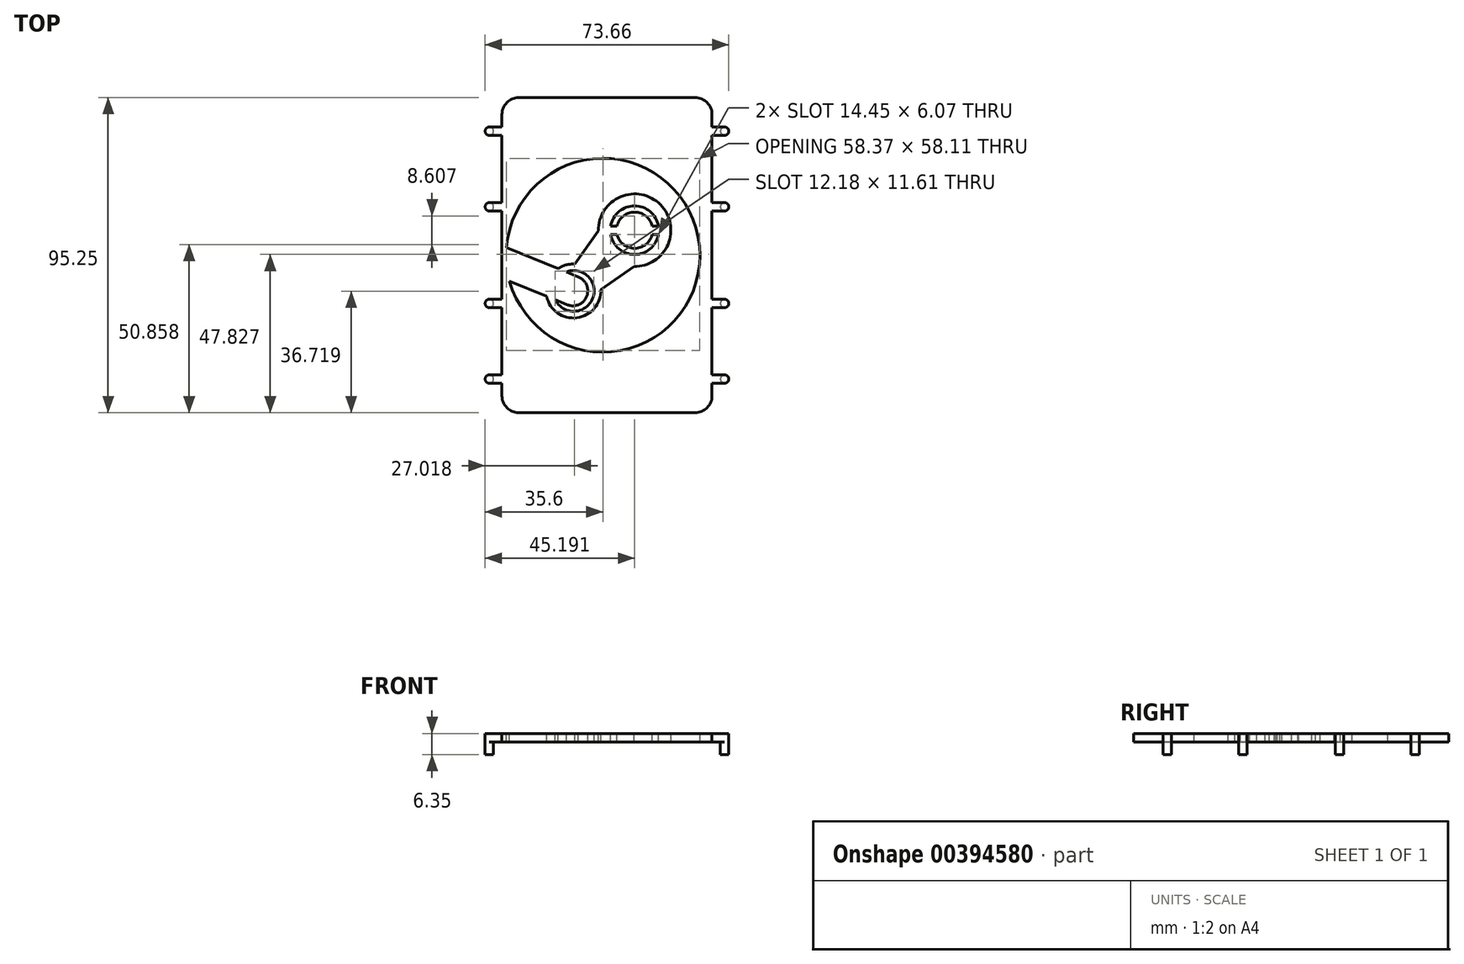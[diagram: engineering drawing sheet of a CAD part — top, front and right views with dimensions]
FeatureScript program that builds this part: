
annotation { "Feature Type Name" : "Feature", "Feature Type Description" : "" }
export const myFeature = defineFeature(function(context is Context, id is Id, definition is map)
    precondition{}
    {
        {
            var Q0;
            Q0=qCreatedBy(makeId("Top.planeOp"),FACE);
            var sketch = newSketch(context, id + "F0", { "sketchPlane" : qUnion([Q0])});
            skLineSegment(sketch, "E0.bottom", {"start": v(-63.5, 95.25) * mm, "end": v(0, 95.25) * mm});
            skLineSegment(sketch, "E0.top", {"start": v(-63.5, 0) * mm, "end": v(0, 0) * mm});
            skLineSegment(sketch, "E0.left", {"start": v(-63.5, 95.25) * mm, "end": v(-63.5, 0) * mm});
            skLineSegment(sketch, "E0.right", {"start": v(0, 95.25) * mm, "end": v(0, 0) * mm});
            skSolve(sketch);
        }
        {
            var Q0;
            Q0=makeQuery(id+"F0.imprint","IMPRINT",FACE,{"disambiguationData":[TD([[makeQuery(id+"F0.imprint","IMPRINT",EDGE,{"derivedFrom":sQuery(id+"F0.wireOp",EDGE,"E0.bottom")}),-1.0]])]});
            extrude(context, id + "F1", {"entities" : qUnion([Q0]), "depth" : 2.54 * mm});
        }
        {
            var Q0;
            Q0=makeQuery(id+"F1.opExtrude","SWEPT_EDGE",EDGE,{"disambiguationData":[OSD([sQuery(id+"F0.wireOp",EDGE,"E0.top"),sQuery(id+"F0.wireOp",EDGE,"E0.left")])]});
            var Q1;
            Q1=makeQuery(id+"F1.opExtrude","SWEPT_EDGE",EDGE,{"disambiguationData":[OSD([sQuery(id+"F0.wireOp",EDGE,"E0.top"),sQuery(id+"F0.wireOp",EDGE,"E0.right")])]});
            var Q2;
            Q2=makeQuery(id+"F1.opExtrude","SWEPT_EDGE",EDGE,{"disambiguationData":[OSD([sQuery(id+"F0.wireOp",EDGE,"E0.bottom"),sQuery(id+"F0.wireOp",EDGE,"E0.right")])]});
            var Q3;
            Q3=makeQuery(id+"F1.opExtrude","SWEPT_EDGE",EDGE,{"disambiguationData":[OSD([sQuery(id+"F0.wireOp",EDGE,"E0.bottom"),sQuery(id+"F0.wireOp",EDGE,"E0.left")])]});
            fillet(context, id + "F2", {"entities" : qUnion([Q0, Q1, Q2, Q3]), "radius" : 5.08 * mm, "tangentPropagation" : true, "allowEdgeOverflow" : false});
        }
        {
            var Q0;
            Q0=makeQuery(id+"F1.opExtrude","CAP_FACE",FACE,{"disambiguationData":[OSD([sQuery(id+"F0.wireOp",EDGE,"E0.bottom"),sQuery(id+"F0.wireOp",EDGE,"E0.top"),sQuery(id+"F0.wireOp",EDGE,"E0.left"),sQuery(id+"F0.wireOp",EDGE,"E0.right")])],"isStart":false});
            var sketch = newSketch(context, id + "F3", { "sketchPlane" : qUnion([Q0])});
            skPoint(sketch, "E1", {"position": v(0, 47.63) * mm});
            skLineSegment(sketch, "E2", {"start": v(-62.17, 49.9) * mm, "end": v(-46.54, 43.5) * mm});
            skArc(sketch, "E3", {"start": v(-41.49, 44.9) * mm, "mid": v(-44.14, 44.65) * mm, "end": v(-46.54, 43.5) * mm});
            skLineSegment(sketch, "E4", {"start": v(-41.49, 44.9) * mm, "end": v(-34.35, 55.05) * mm});
            skArc(sketch, "E5", {"start": v(-23.6, 44.2) * mm, "mid": v(-15.6, 62.88) * mm, "end": v(-34.35, 55.05) * mm});
            skCircle(sketch, "E6", {"center": v(-23.39, 55.16) * mm, "radius": 5.47 * mm});
            skCircle(sketch, "E7", {"center": v(-23.39, 55.16) * mm, "radius": 7.34 * mm});
            skLineSegment(sketch, "E8", {"start": v(-23.6, 44.2) * mm, "end": v(-33.57, 37.24) * mm});
            skArc(sketch, "E9", {"start": v(-49.98, 35.15) * mm, "mid": v(-40.82, 28.7) * mm, "end": v(-33.57, 37.24) * mm});
            skLineSegment(sketch, "E10", {"start": v(-49.98, 35.15) * mm, "end": v(-61.2, 39.82) * mm});
            skArc(sketch, "E11", {"start": v(-61.2, 39.82) * mm, "mid": v(-3.8, 50.35) * mm, "end": v(-62.17, 49.9) * mm});
            skLineSegment(sketch, "E12", {"start": v(-44, 42.55) * mm, "end": v(-40.45, 41.06) * mm});
            skLineSegment(sketch, "E13", {"start": v(-47.37, 34.15) * mm, "end": v(-43.83, 32.66) * mm});
            skArc(sketch, "E14", {"start": v(-43.83, 32.66) * mm, "mid": v(-37.87, 35.15) * mm, "end": v(-40.45, 41.06) * mm});
            skArc(sketch, "E15", {"start": v(-47.37, 34.15) * mm, "mid": v(-36.08, 34.5) * mm, "end": v(-44, 42.55) * mm});
            skLineSegment(sketch, "E16", {"start": v(-30.62, 56.43) * mm, "end": v(-28.71, 56.43) * mm});
            skLineSegment(sketch, "E17", {"start": v(-30.62, 53.9) * mm, "end": v(-28.71, 53.9) * mm});
            skLineSegment(sketch, "E18", {"start": v(-16.16, 53.9) * mm, "end": v(-18.06, 53.9) * mm});
            skLineSegment(sketch, "E19", {"start": v(-18.06, 56.43) * mm, "end": v(-16.16, 56.43) * mm});
            skSolve(sketch);
        }
        {
            var Q0;
            {var subQ0=sQuery(id+"F3.wireOp",EDGE,"E16");Q0=makeQuery(id+"F3.imprint","IMPRINT",FACE,{"disambiguationData":[TD([[makeQuery(id+"F3.imprint","IMPRINT",EDGE,{"derivedFrom":subQ0}),1.0]])]});}
            var Q1;
            {var subQ0=sQuery(id+"F3.wireOp",EDGE,"E17");Q1=makeQuery(id+"F3.imprint","IMPRINT",FACE,{"disambiguationData":[TD([[makeQuery(id+"F3.imprint","IMPRINT",EDGE,{"derivedFrom":subQ0}),-1.0]])]});}
            var Q2;
            Q2=makeQuery(id+"F3.imprint","IMPRINT",FACE,{"disambiguationData":[TD([[makeQuery(id+"F3.imprint","IMPRINT",EDGE,{"derivedFrom":sQuery(id+"F3.wireOp",EDGE,"E2")}),1.0]])]});
            var Q3;
            Q3=makeQuery(id+"F3.imprint","IMPRINT",FACE,{"disambiguationData":[TD([[makeQuery(id+"F3.imprint","IMPRINT",EDGE,{"derivedFrom":sQuery(id+"F3.wireOp",EDGE,"E12")}),1.0]])]});
            extrude(context, id + "F4", {"entities" : qUnion([Q0, Q1, Q2, Q3]), "operationType" : NewBodyOperationType.REMOVE, "endBound" : BoundingType.THROUGH_ALL, "oppositeDirection" : true, "depth" : 2.54 * mm});
        }
        {
            var Q0;
            {var subQ0=sQuery(id+"F0.wireOp",EDGE,"E0.right");var subQ1=sQuery(id+"F0.wireOp",EDGE,"E0.top");var subQ2=sQuery(id+"F0.wireOp",EDGE,"E0.left");var subQ3=sQuery(id+"F0.wireOp",EDGE,"E0.bottom");Q0=makeQuery(id+"F4.boolean.opBoolean","SPLIT",FACE,{"disambiguationData":[TD([makeQuery(id+"F1.opExtrude","SWEPT_FACE",FACE,{"disambiguationData":[OSD([subQ3])]})])],"derivedFrom":makeQuery(id+"F1.opExtrude","CAP_FACE",FACE,{"disambiguationData":[OSD([subQ3,subQ1,subQ2,subQ0])],"isStart":true})});}
            var sketch = newSketch(context, id + "F5", { "sketchPlane" : qUnion([Q0])});
            skCircle(sketch, "E20", {"center": v(-67.31, -10.16) * mm, "radius": 1.27 * mm});
            skCircle(sketch, "E21", {"center": v(-67.31, -33.02) * mm, "radius": 1.27 * mm});
            skCircle(sketch, "E22", {"center": v(-67.31, -62.23) * mm, "radius": 1.27 * mm});
            skCircle(sketch, "E23", {"center": v(-67.31, -85.1) * mm, "radius": 1.27 * mm});
            skCircle(sketch, "E24", {"center": v(3.8, -85.1) * mm, "radius": 1.27 * mm});
            skCircle(sketch, "E25", {"center": v(3.8, -62.23) * mm, "radius": 1.27 * mm});
            skCircle(sketch, "E26", {"center": v(3.8, -33.02) * mm, "radius": 1.27 * mm});
            skCircle(sketch, "E27", {"center": v(3.8, -10.16) * mm, "radius": 1.27 * mm});
            skLineSegment(sketch, "E28", {"start": v(-67.31, -86.36) * mm, "end": v(-63.5, -86.36) * mm});
            skLineSegment(sketch, "E29", {"start": v(-63.5, -86.36) * mm, "end": v(-63.5, -83.82) * mm});
            skLineSegment(sketch, "E30", {"start": v(-63.5, -83.82) * mm, "end": v(-67.31, -83.82) * mm});
            skLineSegment(sketch, "E31", {"start": v(-67.31, -63.5) * mm, "end": v(-63.5, -63.5) * mm});
            skLineSegment(sketch, "E32", {"start": v(-63.5, -63.5) * mm, "end": v(-63.5, -60.96) * mm});
            skLineSegment(sketch, "E33", {"start": v(-63.5, -60.96) * mm, "end": v(-67.31, -60.96) * mm});
            skLineSegment(sketch, "E34", {"start": v(-67.31, -34.3) * mm, "end": v(-63.5, -34.3) * mm});
            skLineSegment(sketch, "E35", {"start": v(-63.5, -34.3) * mm, "end": v(-63.5, -31.75) * mm});
            skLineSegment(sketch, "E36", {"start": v(-63.5, -31.75) * mm, "end": v(-67.31, -31.75) * mm});
            skLineSegment(sketch, "E37", {"start": v(-67.31, -11.43) * mm, "end": v(-63.5, -11.43) * mm});
            skLineSegment(sketch, "E38", {"start": v(-67.31, -8.9) * mm, "end": v(-63.5, -8.9) * mm});
            skLineSegment(sketch, "E39", {"start": v(-63.5, -8.9) * mm, "end": v(-63.5, -11.43) * mm});
            skLineSegment(sketch, "E40", {"start": v(3.8, -11.43) * mm, "end": v(0, -11.43) * mm});
            skLineSegment(sketch, "E41", {"start": v(0, -11.43) * mm, "end": v(0, -8.9) * mm});
            skLineSegment(sketch, "E42", {"start": v(0, -8.9) * mm, "end": v(3.8, -8.9) * mm});
            skLineSegment(sketch, "E43", {"start": v(3.8, -34.3) * mm, "end": v(0, -34.3) * mm});
            skLineSegment(sketch, "E44", {"start": v(0, -34.3) * mm, "end": v(0, -31.75) * mm});
            skLineSegment(sketch, "E45", {"start": v(0, -31.75) * mm, "end": v(3.8, -31.75) * mm});
            skLineSegment(sketch, "E46", {"start": v(3.8, -63.5) * mm, "end": v(0, -63.5) * mm});
            skLineSegment(sketch, "E47", {"start": v(0, -63.5) * mm, "end": v(0, -60.96) * mm});
            skLineSegment(sketch, "E48", {"start": v(0, -60.96) * mm, "end": v(3.8, -60.96) * mm});
            skLineSegment(sketch, "E49", {"start": v(3.8, -83.82) * mm, "end": v(0, -83.82) * mm});
            skLineSegment(sketch, "E50", {"start": v(0, -86.36) * mm, "end": v(0, -83.82) * mm});
            skLineSegment(sketch, "E51", {"start": v(0, -86.36) * mm, "end": v(3.8, -86.36) * mm});
            skSolve(sketch);
        }
        {
            var Q0;
            {var subQ0=sQuery(id+"F5.wireOp",EDGE,"E28");Q0=makeQuery(id+"F5.imprint","IMPRINT",FACE,{"disambiguationData":[TD([[makeQuery(id+"F5.imprint","IMPRINT",EDGE,{"derivedFrom":subQ0}),1.0]])]});}
            var Q1;
            {var subQ0=sQuery(id+"F5.wireOp",EDGE,"E31");Q1=makeQuery(id+"F5.imprint","IMPRINT",FACE,{"disambiguationData":[TD([[makeQuery(id+"F5.imprint","IMPRINT",EDGE,{"derivedFrom":subQ0}),1.0]])]});}
            var Q2;
            {var subQ0=sQuery(id+"F5.wireOp",EDGE,"E34");Q2=makeQuery(id+"F5.imprint","IMPRINT",FACE,{"disambiguationData":[TD([[makeQuery(id+"F5.imprint","IMPRINT",EDGE,{"derivedFrom":subQ0}),1.0]])]});}
            var Q3;
            {var subQ0=sQuery(id+"F5.wireOp",EDGE,"E37");Q3=makeQuery(id+"F5.imprint","IMPRINT",FACE,{"disambiguationData":[TD([[makeQuery(id+"F5.imprint","IMPRINT",EDGE,{"derivedFrom":subQ0}),1.0]])]});}
            var Q4;
            {var subQ0=sQuery(id+"F5.wireOp",EDGE,"E40");Q4=makeQuery(id+"F5.imprint","IMPRINT",FACE,{"disambiguationData":[TD([[makeQuery(id+"F5.imprint","IMPRINT",EDGE,{"derivedFrom":subQ0}),-1.0]])]});}
            var Q5;
            {var subQ0=sQuery(id+"F5.wireOp",EDGE,"E43");Q5=makeQuery(id+"F5.imprint","IMPRINT",FACE,{"disambiguationData":[TD([[makeQuery(id+"F5.imprint","IMPRINT",EDGE,{"derivedFrom":subQ0}),-1.0]])]});}
            var Q6;
            {var subQ0=sQuery(id+"F5.wireOp",EDGE,"E46");Q6=makeQuery(id+"F5.imprint","IMPRINT",FACE,{"disambiguationData":[TD([[makeQuery(id+"F5.imprint","IMPRINT",EDGE,{"derivedFrom":subQ0}),-1.0]])]});}
            var Q7;
            {var subQ0=sQuery(id+"F5.wireOp",EDGE,"E49");Q7=makeQuery(id+"F5.imprint","IMPRINT",FACE,{"disambiguationData":[TD([[makeQuery(id+"F5.imprint","IMPRINT",EDGE,{"derivedFrom":subQ0}),1.0]])]});}
            extrude(context, id + "F6", {"entities" : qUnion([Q0, Q1, Q2, Q3, Q4, Q5, Q6, Q7]), "operationType" : NewBodyOperationType.ADD, "oppositeDirection" : true, "depth" : 2.54 * mm});
        }
        {
            var Q0;
            {var subQ0=sQuery(id+"F5.wireOp",EDGE,"E23");var subQ1=makeQuery(id+"F5.imprint","INTERSECT",VERTEX,{"derivedFrom":[subQ0,sQuery(id+"F5.wireOp",EDGE,"E28")]});Q0=makeQuery(id+"F5.imprint","IMPRINT",FACE,{"disambiguationData":[TD([[makeQuery(id+"F5.imprint","IMPRINT",EDGE,{"disambiguationData":[TD([[subQ1,1.0]])],"derivedFrom":subQ0}),1.0]])]});}
            var Q1;
            {var subQ0=sQuery(id+"F5.wireOp",EDGE,"E22");var subQ1=makeQuery(id+"F5.imprint","INTERSECT",VERTEX,{"derivedFrom":[subQ0,sQuery(id+"F5.wireOp",EDGE,"E31")]});Q1=makeQuery(id+"F5.imprint","IMPRINT",FACE,{"disambiguationData":[TD([[makeQuery(id+"F5.imprint","IMPRINT",EDGE,{"disambiguationData":[TD([[subQ1,1.0]])],"derivedFrom":subQ0}),1.0]])]});}
            var Q2;
            {var subQ0=sQuery(id+"F5.wireOp",EDGE,"E21");var subQ1=makeQuery(id+"F5.imprint","INTERSECT",VERTEX,{"derivedFrom":[subQ0,sQuery(id+"F5.wireOp",EDGE,"E34")]});Q2=makeQuery(id+"F5.imprint","IMPRINT",FACE,{"disambiguationData":[TD([[makeQuery(id+"F5.imprint","IMPRINT",EDGE,{"disambiguationData":[TD([[subQ1,1.0]])],"derivedFrom":subQ0}),1.0]])]});}
            var Q3;
            {var subQ0=sQuery(id+"F5.wireOp",EDGE,"E20");var subQ1=makeQuery(id+"F5.imprint","INTERSECT",VERTEX,{"derivedFrom":[subQ0,sQuery(id+"F5.wireOp",EDGE,"E37")]});Q3=makeQuery(id+"F5.imprint","IMPRINT",FACE,{"disambiguationData":[TD([[makeQuery(id+"F5.imprint","IMPRINT",EDGE,{"disambiguationData":[TD([[subQ1,1.0]])],"derivedFrom":subQ0}),1.0]])]});}
            var Q4;
            {var subQ0=sQuery(id+"F5.wireOp",EDGE,"E27");var subQ1=makeQuery(id+"F5.imprint","INTERSECT",VERTEX,{"derivedFrom":[subQ0,sQuery(id+"F5.wireOp",EDGE,"E40")]});Q4=makeQuery(id+"F5.imprint","IMPRINT",FACE,{"disambiguationData":[TD([[makeQuery(id+"F5.imprint","IMPRINT",EDGE,{"disambiguationData":[TD([[subQ1,1.0]])],"derivedFrom":subQ0}),1.0]])]});}
            var Q5;
            {var subQ0=sQuery(id+"F5.wireOp",EDGE,"E26");var subQ1=makeQuery(id+"F5.imprint","INTERSECT",VERTEX,{"derivedFrom":[subQ0,sQuery(id+"F5.wireOp",EDGE,"E43")]});Q5=makeQuery(id+"F5.imprint","IMPRINT",FACE,{"disambiguationData":[TD([[makeQuery(id+"F5.imprint","IMPRINT",EDGE,{"disambiguationData":[TD([[subQ1,1.0]])],"derivedFrom":subQ0}),1.0]])]});}
            var Q6;
            {var subQ0=sQuery(id+"F5.wireOp",EDGE,"E25");var subQ1=makeQuery(id+"F5.imprint","INTERSECT",VERTEX,{"derivedFrom":[subQ0,sQuery(id+"F5.wireOp",EDGE,"E46")]});Q6=makeQuery(id+"F5.imprint","IMPRINT",FACE,{"disambiguationData":[TD([[makeQuery(id+"F5.imprint","IMPRINT",EDGE,{"disambiguationData":[TD([[subQ1,1.0]])],"derivedFrom":subQ0}),1.0]])]});}
            var Q7;
            {var subQ0=sQuery(id+"F5.wireOp",EDGE,"E24");var subQ1=makeQuery(id+"F5.imprint","INTERSECT",VERTEX,{"derivedFrom":[subQ0,sQuery(id+"F5.wireOp",EDGE,"E49")]});Q7=makeQuery(id+"F5.imprint","IMPRINT",FACE,{"disambiguationData":[TD([[makeQuery(id+"F5.imprint","IMPRINT",EDGE,{"disambiguationData":[TD([[subQ1,-1.0]])],"derivedFrom":subQ0}),1.0]])]});}
            extrude(context, id + "F7", {"entities" : qUnion([Q0, Q1, Q2, Q3, Q4, Q5, Q6, Q7]), "operationType" : NewBodyOperationType.ADD, "oppositeDirection" : true, "depth" : 2.54 * mm, "hasSecondDirection" : true, "secondDirectionOppositeDirection" : false, "secondDirectionDepth" : 3.8 * mm});
        }
    });
